# Revit family: TCNHU-B
name_source: partatom
category: Mechanical Equipment
units: mm (PartAtom-declared; Revit-internal decimal feet)

## family parameters
Always vertical = Yes
Cut with Voids When Loaded = No
Part Type = Normal
Room Calculation Point = No
Round Connector Dimension = Use Diameter
Shared = No
Work Plane-Based = No

## types (20) — shared parameters
0 = 0' - 0"
1" = 0' - 1"
1.5 = 0' - 1 1/2"
2" = 0' - 2"
2' = 2' - 0"
3" = 0' - 3"
4" = 0' - 4"
5" = 0' - 5"
Manufacturer = Loren Cook Company
Model = TCNHU-B
ONE EIGTH = 0' - 0 1/8"
Type Comments = Tubular Centrifugal Upblast Roof Mounted / Exhaust Belt Drive
URL = www.lorencook.com

## per-type parameters (varying)
| type | (B/2)-.5" | (D+.25")/2 | (T_SQ/2)+.125" | A | A-.5" | B | C | C/2 | D | D/2 | E | E+A-1" | E+A-1"-G | F | FAN_DIA | FAN_RAD | G | H | J | J/2 | RO | RO/2 | T_SQ | T_SQ/2 |
| 100_TCNHU-B | 0' - 6 15/16" | 0' - 8 1/8" | 1' - 0 1/8" | 1' - 10" | 1' - 9 1/2" | 1' - 2 7/8" | 1' - 7" | 0' - 9 1/2" | 1' - 4" | 0' - 8" | 0' - 3" | 2' - 0" | 0' - 6" | 2' - 9 1/4" | 1' - 4" | 0' - 8" | 1' - 6" | 3' - 3 7/8" | 1' - 1" | 0' - 6 1/2" | 1' - 7 1/2" | 0' - 9 3/4" | 2' - 0" | 1' - 0" |
| 120_TCNHU-B | 0' - 7 15/32" | 0' - 9 1/8" | 1' - 0 1/8" | 1' - 11" | 1' - 10 1/2" | 1' - 3 15/16" | 1' - 9" | 0' - 10 1/2" | 1' - 6" | 0' - 9" | 0' - 3" | 2' - 1" | 0' - 7" | 2' - 11" | 1' - 6" | 0' - 9" | 1' - 6" | 3' - 5 15/16" | 1' - 1" | 0' - 6 1/2" | 1' - 7 1/2" | 0' - 9 3/4" | 2' - 0" | 1' - 0" |
| 135_TCNHU-B | 0' - 8 1/2" | 0' - 10 5/8" | 1' - 2 1/8" | 2' - 0 1/2" | 2' - 0" | 1' - 6" | 2' - 0" | 1' - 0" | 1' - 9" | 0' - 10 1/2" | 0' - 3" | 2' - 2 1/2" | 0' - 8 1/2" | 3' - 3 1/8" | 1' - 9" | 0' - 10 1/2" | 1' - 6" | 3' - 9 1/2" | 1' - 1" | 0' - 6 1/2" | 1' - 11 1/2" | 0' - 11 3/4" | 2' - 4" | 1' - 2" |
| 150_TCNHU-B | 0' - 9 15/32" | 1' - 0 1/8" | 1' - 3 1/8" | 2' - 3" | 2' - 2 1/2" | 1' - 7 15/16" | 2' - 3" | 1' - 1 1/2" | 2' - 0" | 1' - 0" | 0' - 3" | 2' - 5" | 0' - 7" | 3' - 5 3/4" | 2' - 0" | 1' - 0" | 1' - 10" | 4' - 1 15/16" | 1' - 4 3/4" | 0' - 8 3/8" | 2' - 1 1/2" | 1' - 0 3/4" | 2' - 6" | 1' - 3" |
| 165_TCNHU-B | 0' - 9 15/16" | 1' - 1 1/8" | 1' - 3 1/8" | 2' - 4 1/2" | 2' - 4" | 1' - 8 7/8" | 2' - 5" | 1' - 2 1/2" | 2' - 2" | 1' - 1" | 0' - 3" | 2' - 6 1/2" | 0' - 8 1/2" | 3' - 7 3/16" | 2' - 2" | 1' - 1" | 1' - 10" | 4' - 4 3/8" | 1' - 4 3/4" | 0' - 8 3/8" | 2' - 1 1/2" | 1' - 0 3/4" | 2' - 6" | 1' - 3" |
| 180_TCNHU-B | 0' - 10 17/32" | 1' - 2 1/8" | 1' - 6 1/8" | 2' - 7" | 2' - 6 1/2" | 1' - 10 1/16" | 2' - 7" | 1' - 3 1/2" | 2' - 4" | 1' - 2" | 0' - 3" | 2' - 9" | 0' - 11" | 3' - 11 9/16" | 2' - 4" | 1' - 2" | 1' - 10" | 4' - 8 1/16" | 1' - 4 3/4" | 0' - 8 3/8" | 2' - 7 1/2" | 1' - 3 3/4" | 3' - 0" | 1' - 6" |
| 195_TCNHU-B | 0' - 11 23/32" | 1' - 3 5/8" | 1' - 7 1/8" | 2' - 9 1/4" | 2' - 8 3/4" | 2' - 0 7/16" | 2' - 10" | 1' - 5" | 2' - 7" | 1' - 3 1/2" | 0' - 3" | 2' - 11 1/4" | 1' - 1 1/4" | 4' - 2 7/16" | 2' - 7" | 1' - 3 1/2" | 1' - 10" | 5' - 0 11/16" | 1' - 4 3/4" | 0' - 8 3/8" | 2' - 9 1/2" | 1' - 4 3/4" | 3' - 2" | 1' - 7" |
| 210_TCNHU-B | 1' - 0 25/32" | 1' - 5 1/8" | 1' - 9 1/8" | 2' - 10 1/2" | 2' - 10" | 2' - 2 9/16" | 3' - 1" | 1' - 6 1/2" | 2' - 10" | 1' - 5" | 0' - 3" | 3' - 0 1/2" | 1' - 2 1/2" | 4' - 6 1/4" | 2' - 10" | 1' - 5" | 1' - 10" | 5' - 4 1/16" | 1' - 4 3/4" | 0' - 8 3/8" | 3' - 1 1/2" | 1' - 6 3/4" | 3' - 6" | 1' - 9" |
| 225_TCNHU-B | 1' - 1 1/8" | 1' - 6 1/8" | 1' - 9 1/8" | 2' - 11 1/2" | 2' - 11" | 2' - 3 1/4" | 3' - 4 1/4" | 1' - 8 1/8" | 3' - 0" | 1' - 6" | 0' - 3" | 3' - 1 1/2" | 1' - 0 1/2" | 4' - 11" | 3' - 0" | 1' - 6" | 2' - 1" | 5' - 5 3/4" | 1' - 6" | 0' - 9" | 3' - 1 1/2" | 1' - 6 3/4" | 3' - 6" | 1' - 9" |
| 245_TCNHU-B | 1' - 2 5/16" | 1' - 8 1/8" | 2' - 0 1/8" | 3' - 5" | 3' - 4 1/2" | 2' - 5 5/8" | 3' - 8 1/4" | 1' - 10 1/8" | 3' - 4" | 1' - 8" | 0' - 3" | 3' - 7" | 1' - 6" | 5' - 4 5/16" | 3' - 4" | 1' - 8" | 2' - 1" | 6' - 1 5/8" | 1' - 6" | 0' - 9" | 3' - 7 1/2" | 1' - 9 3/4" | 4' - 0" | 2' - 0" |
| 270_TCNHU-B | 1' - 3 3/4" | 1' - 10 1/8" | 2' - 3 1/8" | 3' - 10 1/2" | 3' - 10" | 2' - 8 1/2" | 4' - 0 1/4" | 2' - 0 1/8" | 3' - 8" | 1' - 10" | 0' - 3" | 4' - 0 1/2" | 1' - 6 1/2" | 5' - 11 11/16" | 3' - 8" | 1' - 10" | 2' - 6" | 6' - 10" | 1' - 9" | 0' - 10 1/2" | 4' - 1 1/2" | 2' - 0 3/4" | 4' - 6" | 2' - 3" |
| 300_TCNHU-B | 1' - 5 5/32" | 2' - 0 1/8" | 2' - 3 1/8" | 4' - 0 1/4" | 3' - 11 3/4" | 2' - 11 5/16" | 4' - 4 1/4" | 2' - 2 1/8" | 4' - 0" | 2' - 0" | 0' - 3" | 4' - 2 1/4" | 1' - 8 1/4" | 6' - 1 15/16" | 4' - 0" | 2' - 0" | 2' - 6" | 7' - 2 9/16" | 1' - 9" | 0' - 10 1/2" | 4' - 1 1/2" | 2' - 0 3/4" | 4' - 6" | 2' - 3" |
| 60_TCNHU-B | 0' - 6 15/16" | 0' - 8 1/8" | 1' - 0 1/8" | 1' - 10" | 1' - 9 1/2" | 1' - 2 7/8" | 1' - 7" | 0' - 9 1/2" | 1' - 4" | 0' - 8" | 0' - 3" | 2' - 0" | 0' - 6" | 2' - 9 1/4" | 1' - 4" | 0' - 8" | 1' - 6" | 3' - 3 7/8" | 1' - 1" | 0' - 6 1/2" | 1' - 7 1/2" | 0' - 9 3/4" | 2' - 0" | 1' - 0" |
| 70_TCNHU-B | 0' - 6 15/16" | 0' - 8 1/8" | 1' - 0 1/8" | 1' - 10" | 1' - 9 1/2" | 1' - 2 7/8" | 1' - 7" | 0' - 9 1/2" | 1' - 4" | 0' - 8" | 0' - 3" | 2' - 0" | 0' - 6" | 2' - 9 1/4" | 1' - 4" | 0' - 8" | 1' - 6" | 3' - 3 7/8" | 1' - 1" | 0' - 6 1/2" | 1' - 7 1/2" | 0' - 9 3/4" | 2' - 0" | 1' - 0" |
| 80_TCNHU-B | 0' - 6 15/16" | 0' - 8 1/8" | 1' - 0 1/8" | 1' - 10" | 1' - 9 1/2" | 1' - 2 7/8" | 1' - 7" | 0' - 9 1/2" | 1' - 4" | 0' - 8" | 0' - 3" | 2' - 0" | 0' - 6" | 2' - 9 1/4" | 1' - 4" | 0' - 8" | 1' - 6" | 3' - 3 7/8" | 1' - 1" | 0' - 6 1/2" | 1' - 7 1/2" | 0' - 9 3/4" | 2' - 0" | 1' - 0" |
| 330_TCNHU-B | 1' - 6 3/32" | 2' - 2 1/8" | 2' - 6 1/8" | 4' - 4" | 4' - 3 1/2" | 3' - 1 3/16" | 4' - 8 1/4" | 2' - 4 1/8" | 4' - 4" | 2' - 2" | 0' - 3" | 4' - 6" | 2' - 0" | 6' - 7 3/16" | 4' - 4" | 2' - 2" | 2' - 6" | 7' - 8 3/16" | 1' - 9" | 0' - 10 1/2" | 4' - 7 1/2" | 2' - 3 3/4" | 5' - 0" | 2' - 6" |
| 365_TCNHU-B | 1' - 6 25/32" | 2' - 3 1/8" | 2' - 7 1/8" | 4' - 6" | 4' - 5 1/2" | 3' - 2 9/16" | 4' - 10 1/4" | 2' - 5 1/8" | 4' - 6" | 2' - 3" | 0' - 3" | 4' - 8" | 2' - 2" | 6' - 9 3/8" | 4' - 6" | 2' - 3" | 2' - 6" | 7' - 11 9/16" | 1' - 9" | 0' - 10 1/2" | 4' - 9 1/2" | 2' - 4 3/4" | 5' - 2" | 2' - 7" |
| 402_TCNHU-B | 1' - 9" | 2' - 6 1/8" | 3' - 0 1/8" | 4' - 11 1/2" | 4' - 11" | 3' - 7" | 5' - 4 1/4" | 2' - 8 1/8" | 5' - 0" | 2' - 6" | 0' - 3" | 5' - 1 1/2" | 1' - 9 1/2" | 7' - 9 3/8" | 5' - 0" | 2' - 6" | 3' - 4" | 8' - 9 1/2" | 2' - 2" | 1' - 1" | 5' - 7 1/2" | 2' - 9 3/4" | 6' - 0" | 3' - 0" |
| 445_TCNHU-B | 1' - 10 17/32" | 2' - 9 1/8" | 3' - 2 1/8" | 5' - 6" | 5' - 5 1/2" | 3' - 10 1/16" | 5' - 10 1/4" | 2' - 11 1/8" | 5' - 6" | 2' - 9" | 0' - 3" | 5' - 8" | 2' - 4" | 8' - 2 11/16" | 5' - 6" | 2' - 9" | 3' - 4" | 9' - 7 1/16" | 2' - 2" | 1' - 1" | 5' - 11 1/2" | 2' - 11 3/4" | 6' - 4" | 3' - 2" |
| 490_TCNHU-B | 2' - 1 3/16" | 3' - 0 5/8" | 3' - 6 1/8" | 6' - 0 1/2" | 6' - 0" | 4' - 3 3/8" | 6' - 5 1/4" | 3' - 2 5/8" | 6' - 1" | 3' - 0 1/2" | 0' - 4" | 6' - 3 1/2" | 2' - 11 1/2" | 8' - 10 1/2" | 6' - 1" | 3' - 0 1/2" | 3' - 4" | 10' - 7 7/8" | 2' - 2" | 1' - 1" | 6' - 7 1/2" | 3' - 3 3/4" | 7' - 0" | 3' - 6" |

## geometry (parser evidence)
native form markers: Sweep x1
no freeform markers — native parametric forms only
